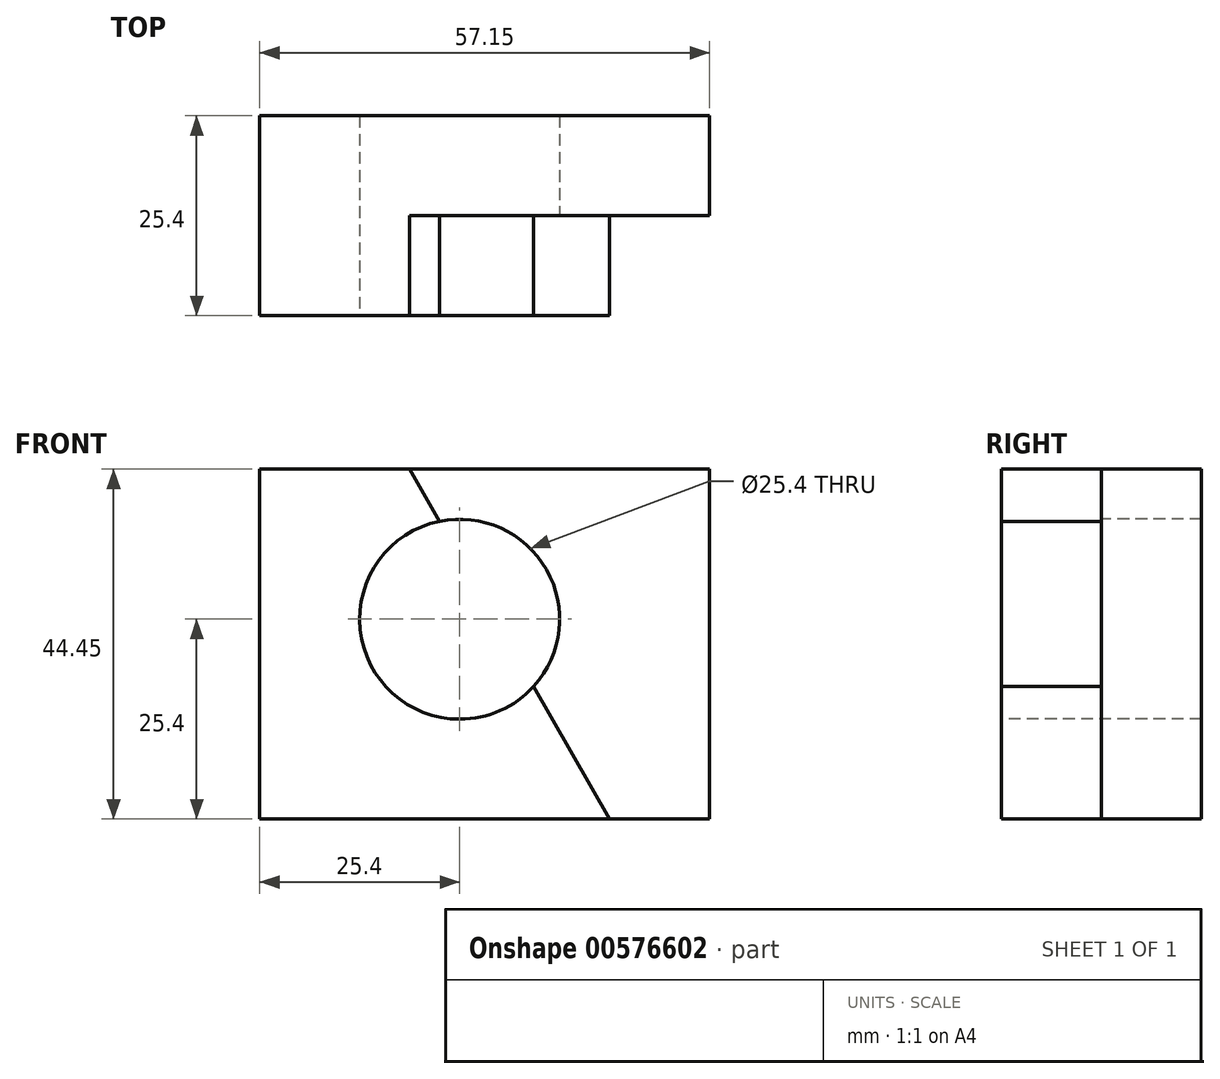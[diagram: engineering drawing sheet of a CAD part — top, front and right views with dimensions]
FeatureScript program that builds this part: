
annotation { "Feature Type Name" : "Feature", "Feature Type Description" : "" }
export const myFeature = defineFeature(function(context is Context, id is Id, definition is map)
    precondition{}
    {
        {
            var Q0;
            Q0=qCreatedBy(makeId("Front.planeOp"),FACE);
            var sketch = newSketch(context, id + "F0", { "sketchPlane" : qUnion([Q0])});
            skLineSegment(sketch, "E0", {"start": v(0, 0) * mm, "end": v(57.15, 0) * mm});
            skLineSegment(sketch, "E1", {"start": v(57.15, 44.45) * mm, "end": v(57.15, 0) * mm});
            skLineSegment(sketch, "E2", {"start": v(57.15, 44.45) * mm, "end": v(0, 44.45) * mm});
            skLineSegment(sketch, "E3", {"start": v(0, 44.45) * mm, "end": v(0, 0) * mm});
            skSolve(sketch);
        }
        {
            var Q0;
            Q0=makeQuery(id+"F0.imprint","IMPRINT",FACE,{"disambiguationData":[TD([[makeQuery(id+"F0.imprint","IMPRINT",EDGE,{"derivedFrom":sQuery(id+"F0.wireOp",EDGE,"E0")}),1.0]])]});
            extrude(context, id + "F1", {"entities" : qUnion([Q0]), "depth" : 25.4 * mm, "offsetDistance" : 25.4 * mm});
        }
        {
            var Q0;
            Q0=makeQuery(id+"F1.opExtrude","CAP_FACE",FACE,{"disambiguationData":[OSD([sQuery(id+"F0.wireOp",EDGE,"E0"),sQuery(id+"F0.wireOp",EDGE,"E1"),sQuery(id+"F0.wireOp",EDGE,"E2"),sQuery(id+"F0.wireOp",EDGE,"E3")])],"isStart":false});
            var sketch = newSketch(context, id + "F2", { "sketchPlane" : qUnion([Q0])});
            skCircle(sketch, "E4", {"center": v(25.4, 25.4) * mm, "radius": 12.7 * mm});
            skSolve(sketch);
        }
        {
            var Q0;
            Q0=makeQuery(id+"F2.imprint","IMPRINT",FACE,{"disambiguationData":[TD([[makeQuery(id+"F2.imprint","IMPRINT",EDGE,{"derivedFrom":sQuery(id+"F2.wireOp",EDGE,"E4")}),1.0]])]});
            extrude(context, id + "F3", {"entities" : qUnion([Q0]), "operationType" : NewBodyOperationType.REMOVE, "oppositeDirection" : true, "depth" : 25.4 * mm, "offsetDistance" : 25.4 * mm});
        }
        {
            var Q0;
            Q0=makeQuery(id+"F1.opExtrude","CAP_FACE",FACE,{"disambiguationData":[OSD([sQuery(id+"F0.wireOp",EDGE,"E0"),sQuery(id+"F0.wireOp",EDGE,"E1"),sQuery(id+"F0.wireOp",EDGE,"E2"),sQuery(id+"F0.wireOp",EDGE,"E3")])],"isStart":false});
            var sketch = newSketch(context, id + "F4", { "sketchPlane" : qUnion([Q0])});
            skLineSegment(sketch, "E5", {"start": v(0, 44.45) * mm, "end": v(19.05, 44.45) * mm});
            skLineSegment(sketch, "E6", {"start": v(57.15, 0) * mm, "end": v(44.45, 0) * mm});
            skLineSegment(sketch, "E7", {"start": v(19.05, 44.45) * mm, "end": v(44.45, 0) * mm});
            skSolve(sketch);
        }
        {
            var Q0;
            {var subQ1=sQuery(id+"F4.wireOp",EDGE,"E6");Q0=makeQuery(id+"F4.imprint","IMPRINT",FACE,{"disambiguationData":[TD([[makeQuery(id+"F4.imprint","IMPRINT",EDGE,{"derivedFrom":subQ1}),1.0]])]});}
            extrude(context, id + "F5", {"entities" : qUnion([Q0]), "operationType" : NewBodyOperationType.REMOVE, "oppositeDirection" : true, "depth" : 12.7 * mm, "offsetDistance" : 25.4 * mm});
        }
    });
